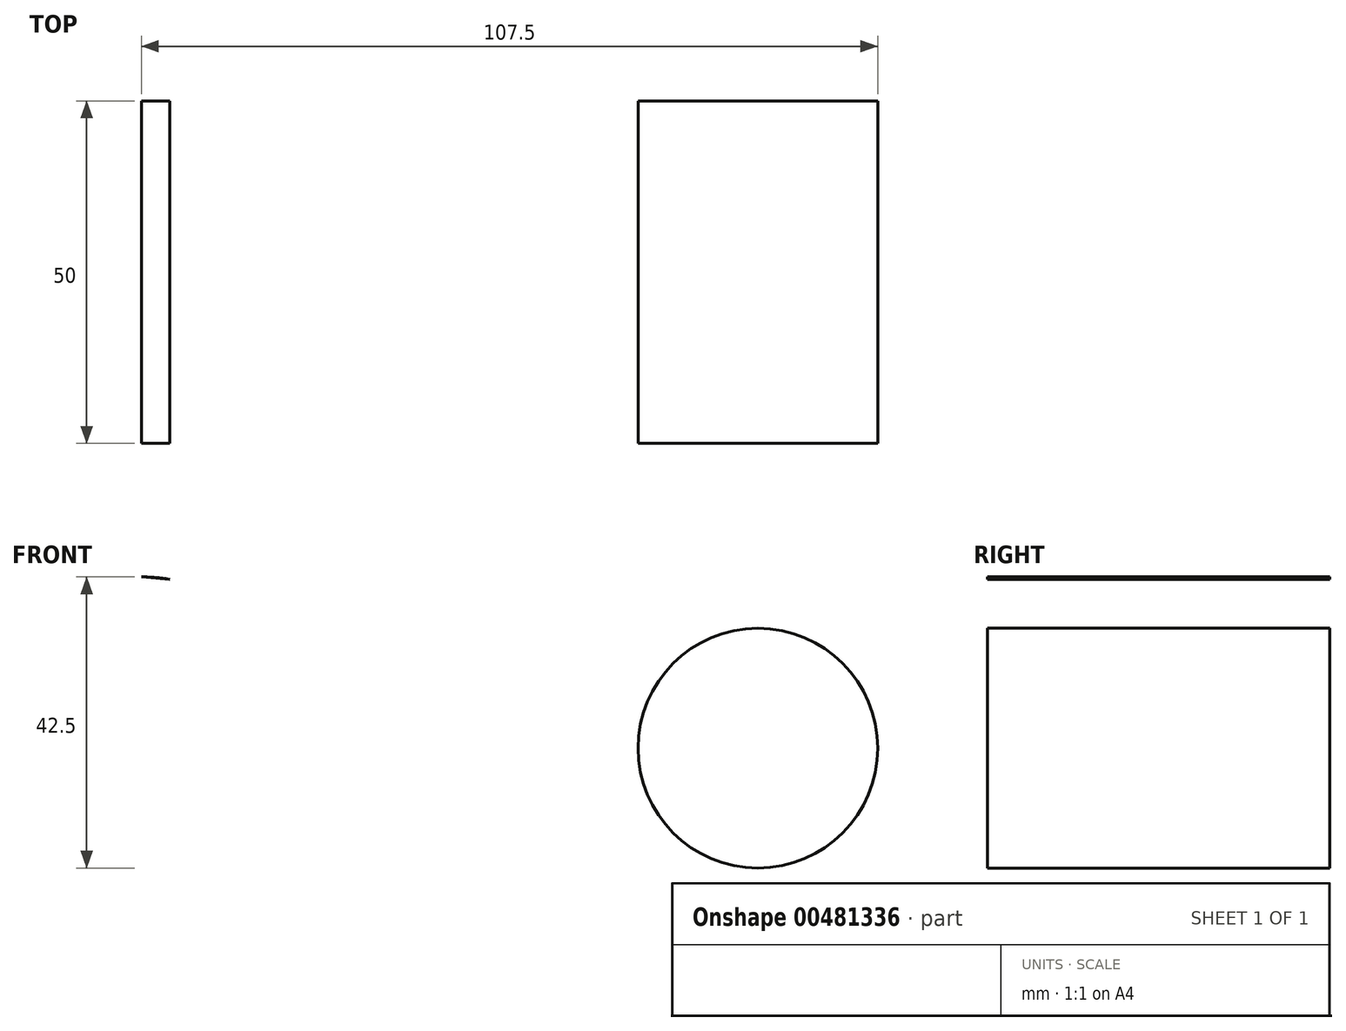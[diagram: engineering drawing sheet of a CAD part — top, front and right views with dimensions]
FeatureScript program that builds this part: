
annotation { "Feature Type Name" : "Feature", "Feature Type Description" : "" }
export const myFeature = defineFeature(function(context is Context, id is Id, definition is map)
    precondition{}
    {
        {
            var Q0;
            Q0=qCreatedBy(makeId("Front.planeOp"),FACE);
            var sketch = newSketch(context, id + "F0", { "sketchPlane" : qUnion([Q0])});
            skCircle(sketch, "E0", {"center": v(0, 0) * mm, "radius": 25 * mm});
            skCircle(sketch, "E1", {"center": v(90, 0) * mm, "radius": 17.5 * mm});
            skLineSegment(sketch, "E2", {"start": v(0, 25) * mm, "end": v(91.44, 17.44) * mm});
            skLineSegment(sketch, "E3", {"start": v(0, -25) * mm, "end": v(91.44, -17.44) * mm});
            skSolve(sketch);
        }
        {
            var Q0;
            {var subQ0=sQuery(id+"F0.wireOp",EDGE,"E2");var subQ1=sQuery(id+"F0.wireOp",EDGE,"E0");var subQ2=makeQuery(id+"F0.imprint","INTERSECT",VERTEX,{"disambiguationData":[OD(1.0)],"derivedFrom":[subQ1,subQ0]});Q0=makeQuery(id+"F0.imprint","IMPRINT",FACE,{"disambiguationData":[TD([[makeQuery(id+"F0.imprint","IMPRINT",EDGE,{"disambiguationData":[TD([[subQ2,1.0]])],"derivedFrom":subQ1}),-1.0]])]});}
            var Q1;
            {var subQ0=sQuery(id+"F0.wireOp",EDGE,"E2");var subQ1=sQuery(id+"F0.wireOp",EDGE,"E0");var subQ2=makeQuery(id+"F0.imprint","INTERSECT",VERTEX,{"disambiguationData":[OD(0.0)],"derivedFrom":[subQ1,subQ0]});Q1=makeQuery(id+"F0.imprint","IMPRINT",FACE,{"disambiguationData":[TD([[makeQuery(id+"F0.imprint","IMPRINT",EDGE,{"disambiguationData":[TD([[subQ2,-1.0]])],"derivedFrom":subQ1}),1.0]])]});}
            var Q2;
            {var subQ0=sQuery(id+"F0.wireOp",EDGE,"E1");var subQ1=makeQuery(id+"F0.imprint","INTERSECT",VERTEX,{"derivedFrom":[subQ0,sQuery(id+"F0.wireOp",EDGE,"E2")]});Q2=makeQuery(id+"F0.imprint","IMPRINT",FACE,{"disambiguationData":[TD([[makeQuery(id+"F0.imprint","IMPRINT",EDGE,{"disambiguationData":[TD([[subQ1,-1.0]])],"derivedFrom":subQ0}),1.0]])]});}
            extrude(context, id + "F1", {"entities" : qUnion([Q0, Q1, Q2]), "depth" : 50 * mm});
        }
    });
